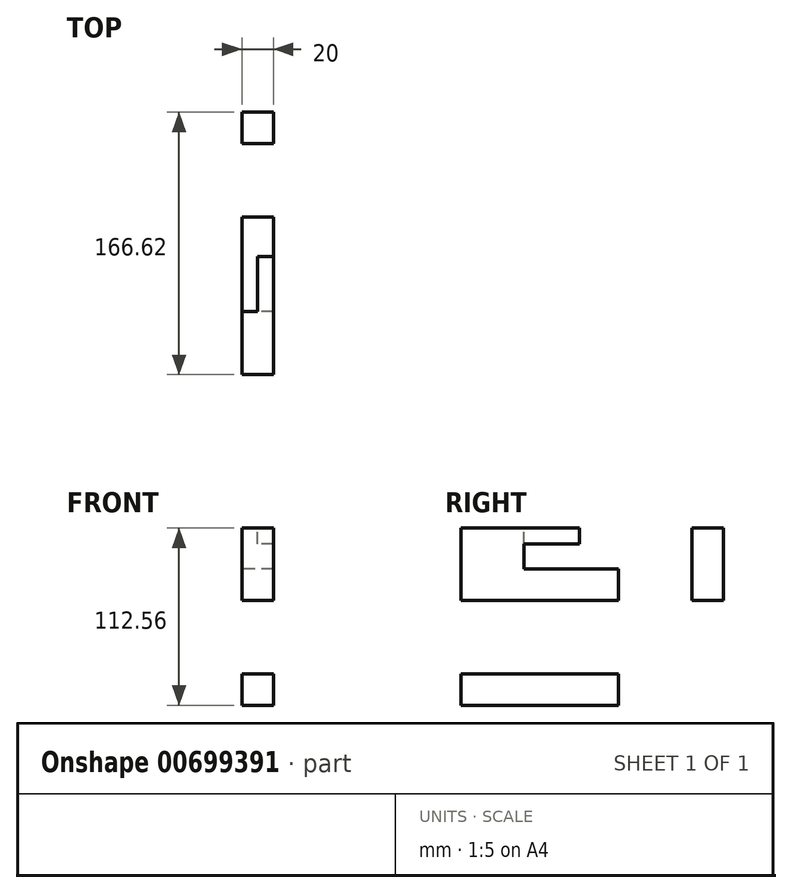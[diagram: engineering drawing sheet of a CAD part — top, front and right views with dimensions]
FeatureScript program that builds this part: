
annotation { "Feature Type Name" : "Feature", "Feature Type Description" : "" }
export const myFeature = defineFeature(function(context is Context, id is Id, definition is map)
    precondition{}
    {
        {
            var Q0;
            Q0=qCreatedBy(makeId("Right.planeOp"),FACE);
            var sketch = newSketch(context, id + "F0", { "sketchPlane" : qUnion([Q0])});
            skLineSegment(sketch, "E0", {"start": v(-554.15, 52.57) * mm, "end": v(-454.15, 52.57) * mm});
            skLineSegment(sketch, "E1", {"start": v(-454.15, 52.57) * mm, "end": v(-454.15, 72.57) * mm});
            skLineSegment(sketch, "E2", {"start": v(-454.15, 72.57) * mm, "end": v(-514.15, 72.57) * mm});
            skLineSegment(sketch, "E3", {"start": v(-514.15, 72.57) * mm, "end": v(-514.15, 88.57) * mm});
            skLineSegment(sketch, "E4", {"start": v(-514.15, 88.57) * mm, "end": v(-479.15, 88.57) * mm});
            skLineSegment(sketch, "E5", {"start": v(-479.15, 88.57) * mm, "end": v(-479.15, 98.57) * mm});
            skLineSegment(sketch, "E6", {"start": v(-514.15, 98.57) * mm, "end": v(-554.15, 98.57) * mm});
            skLineSegment(sketch, "E7", {"start": v(-554.15, 98.57) * mm, "end": v(-554.15, 52.57) * mm});
            skLineSegment(sketch, "E8", {"start": v(-554.15, 6) * mm, "end": v(-554.15, -14) * mm});
            skLineSegment(sketch, "E9", {"start": v(-554.15, -14) * mm, "end": v(-454.15, -14) * mm});
            skLineSegment(sketch, "E10", {"start": v(-454.15, -14) * mm, "end": v(-454.15, 6) * mm});
            skLineSegment(sketch, "E11", {"start": v(-454.15, 6) * mm, "end": v(-554.15, 6) * mm});
            skLineSegment(sketch, "E12", {"start": v(-479.15, -14) * mm, "end": v(-479.15, -1.5) * mm});
            skLineSegment(sketch, "E13", {"start": v(-479.15, -1.5) * mm, "end": v(-514.15, -1.5) * mm});
            skLineSegment(sketch, "E14", {"start": v(-514.15, -1.5) * mm, "end": v(-514.15, -14) * mm, "construction": true});
            skLineSegment(sketch, "E15", {"start": v(-514.15, -1.5) * mm, "end": v(-514.15, 6) * mm});
            skLineSegment(sketch, "E16", {"start": v(-407.53, 52.57) * mm, "end": v(-387.53, 52.57) * mm});
            skLineSegment(sketch, "E17", {"start": v(-387.53, 52.57) * mm, "end": v(-387.53, 98.57) * mm});
            skLineSegment(sketch, "E18", {"start": v(-387.53, 98.57) * mm, "end": v(-407.53, 98.57) * mm});
            skLineSegment(sketch, "E19", {"start": v(-407.53, 98.57) * mm, "end": v(-407.53, 52.57) * mm});
            skLineSegment(sketch, "E20", {"start": v(-407.53, 72.57) * mm, "end": v(-387.53, 72.57) * mm, "construction": true});
            skLineSegment(sketch, "E21", {"start": v(-387.53, 88.57) * mm, "end": v(-400.03, 88.57) * mm, "construction": true});
            skLineSegment(sketch, "E22", {"start": v(-400.03, 88.57) * mm, "end": v(-400.03, 98.57) * mm, "construction": true});
            skLineSegment(sketch, "E23", {"start": v(-514.15, 88.57) * mm, "end": v(-514.15, 98.57) * mm});
            skLineSegment(sketch, "E24", {"start": v(-514.15, 98.57) * mm, "end": v(-479.15, 98.57) * mm});
            skSolve(sketch);
        }
        {
            var Q0;
            Q0 = qSketchRegion(id + "F0", true);
            extrude(context, id + "F1", {"entities" : qUnion([Q0]), "depth" : 20 * mm, "offsetDistance" : 25 * mm});
        }
        {
            var Q0;
            Q0=makeQuery(id+"F0.imprint","IMPRINT",FACE,{"disambiguationData":[TD([[makeQuery(id+"F0.imprint","IMPRINT",EDGE,{"derivedFrom":sQuery(id+"F0.wireOp",EDGE,"E4")}),1.0]])]});
            extrude(context, id + "F2", {"entities" : qUnion([Q0]), "operationType" : NewBodyOperationType.REMOVE, "depth" : 10 * mm, "offsetDistance" : 25 * mm});
        }
    });
